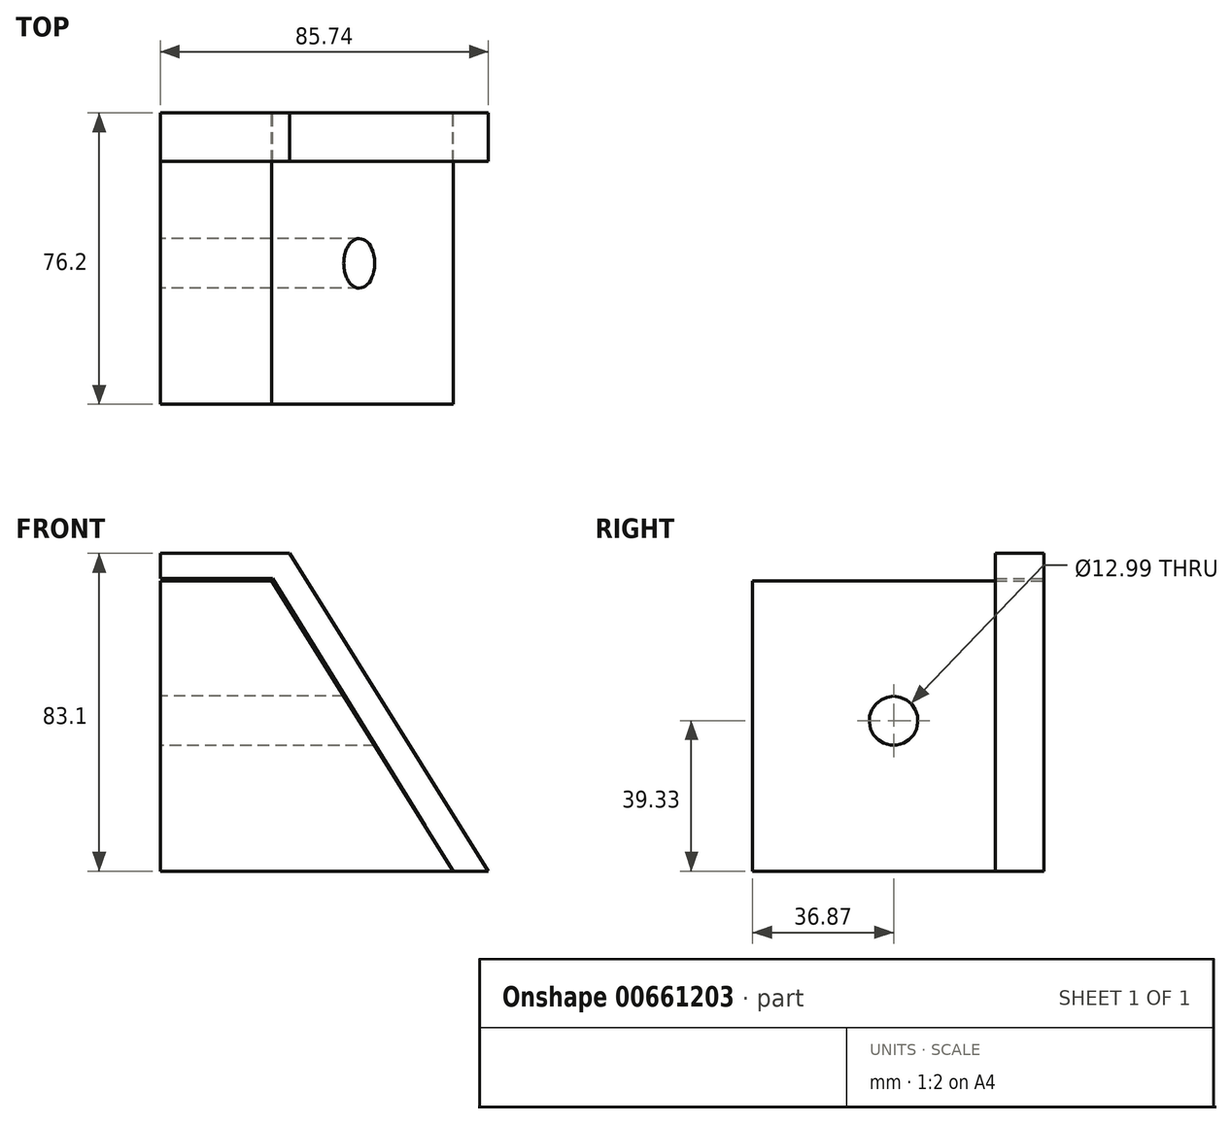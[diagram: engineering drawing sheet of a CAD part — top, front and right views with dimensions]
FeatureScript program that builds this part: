
annotation { "Feature Type Name" : "Feature", "Feature Type Description" : "" }
export const myFeature = defineFeature(function(context is Context, id is Id, definition is map)
    precondition{}
    {
        {
            var Q0;
            Q0=qCreatedBy(makeId("Front.planeOp"),FACE);
            var sketch = newSketch(context, id + "F0", { "sketchPlane" : qUnion([Q0])});
            skLineSegment(sketch, "E0", {"start": v(0, 0) * mm, "end": v(0, 75.96) * mm});
            skLineSegment(sketch, "E1", {"start": v(0, 75.96) * mm, "end": v(29.12, 75.96) * mm});
            skLineSegment(sketch, "E2", {"start": v(29.12, 75.96) * mm, "end": v(76.56, 0) * mm});
            skLineSegment(sketch, "E3", {"start": v(76.56, 0) * mm, "end": v(0, 0) * mm});
            skSolve(sketch);
        }
        {
            var Q0;
            Q0 = qSketchRegion(id + "F0", true);
            extrude(context, id + "F1", {"entities" : qUnion([Q0]), "depth" : 76.2 * mm, "offsetDistance" : 25.4 * mm});
        }
        {
            var Q0;
            Q0=qCreatedBy(makeId("Right.planeOp"),FACE);
            var sketch = newSketch(context, id + "F2", { "sketchPlane" : qUnion([Q0])});
            skCircle(sketch, "E4", {"center": v(-39.33, 39.33) * mm, "radius": 6.5 * mm});
            skSolve(sketch);
        }
        {
            var Q0;
            Q0=makeQuery(id+"F2.imprint","IMPRINT",FACE,{"disambiguationData":[TD([[makeQuery(id+"F2.imprint","IMPRINT",EDGE,{"derivedFrom":sQuery(id+"F2.wireOp",EDGE,"E4")}),1.0]])]});
            extrude(context, id + "F3", {"entities" : qUnion([Q0]), "operationType" : NewBodyOperationType.REMOVE, "depth" : 254 * mm, "offsetDistance" : 25.4 * mm});
        }
        {
            var Q0;
            Q0=qCreatedBy(makeId("Front.planeOp"),FACE);
            var sketch = newSketch(context, id + "F4", { "sketchPlane" : qUnion([Q0])});
            skLineSegment(sketch, "E5", {"start": v(76.44, 0) * mm, "end": v(85.74, 0) * mm});
            skLineSegment(sketch, "E6", {"start": v(85.74, 0) * mm, "end": v(33.85, 83.1) * mm});
            skLineSegment(sketch, "E7", {"start": v(33.85, 83.1) * mm, "end": v(0, 83.1) * mm});
            skLineSegment(sketch, "E8", {"start": v(0, 83.1) * mm, "end": v(0, 76.56) * mm});
            skLineSegment(sketch, "E9", {"start": v(0, 76.56) * mm, "end": v(29.41, 76.56) * mm});
            skLineSegment(sketch, "E10", {"start": v(29.41, 76.56) * mm, "end": v(76.44, 0) * mm});
            skSolve(sketch);
        }
        {
            var Q0;
            Q0 = qSketchRegion(id + "F4", true);
            extrude(context, id + "F5", {"entities" : qUnion([Q0]), "depth" : 12.7 * mm, "offsetDistance" : 25.4 * mm});
        }
    });
